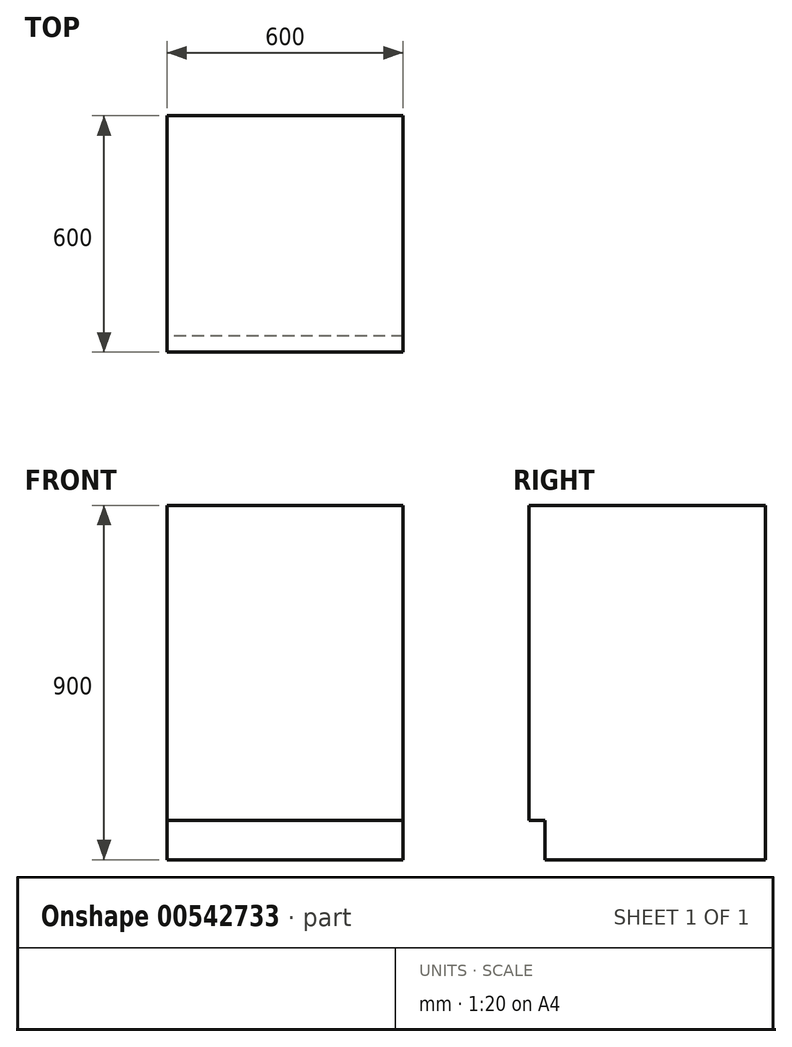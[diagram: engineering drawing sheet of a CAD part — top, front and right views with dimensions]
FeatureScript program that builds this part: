
annotation { "Feature Type Name" : "Feature", "Feature Type Description" : "" }
export const myFeature = defineFeature(function(context is Context, id is Id, definition is map)
    precondition{}
    {
        {
            var Q0;
            Q0=qCreatedBy(makeId("Top.planeOp"),FACE);
            var sketch = newSketch(context, id + "F0", { "sketchPlane" : qUnion([Q0])});
            skLineSegment(sketch, "E0.bottom", {"start": v(300, 300) * mm, "end": v(-300, 300) * mm});
            skLineSegment(sketch, "E0.top", {"start": v(300, -300) * mm, "end": v(-300, -300) * mm});
            skLineSegment(sketch, "E0.left", {"start": v(300, 300) * mm, "end": v(300, -300) * mm});
            skLineSegment(sketch, "E0.right", {"start": v(-300, 300) * mm, "end": v(-300, -300) * mm});
            skPoint(sketch, "E0.middle", {"position": v(0, 0) * mm});
            skSolve(sketch);
        }
        {
            var Q0;
            Q0 = qSketchRegion(id + "F0", true);
            extrude(context, id + "F1", {"entities" : qUnion([Q0]), "depth" : 900 * mm, "offsetDistance" : 25 * mm});
        }
        {
            var Q0;
            Q0=makeQuery(id+"F1.opExtrude","SWEPT_FACE",FACE,{"disambiguationData":[OSD([sQuery(id+"F0.wireOp",EDGE,"E0.top")])]});
            var sketch = newSketch(context, id + "F2", { "sketchPlane" : qUnion([Q0])});
            skLineSegment(sketch, "E1.bottom", {"start": v(-300, 0) * mm, "end": v(300, 0) * mm});
            skLineSegment(sketch, "E1.top", {"start": v(-300, 100) * mm, "end": v(300, 100) * mm});
            skLineSegment(sketch, "E1.left", {"start": v(-300, 0) * mm, "end": v(-300, 100) * mm});
            skLineSegment(sketch, "E1.right", {"start": v(300, 0) * mm, "end": v(300, 100) * mm});
            skSolve(sketch);
        }
        {
            var Q0;
            Q0 = qSketchRegion(id + "F2", true);
            extrude(context, id + "F3", {"entities" : qUnion([Q0]), "operationType" : NewBodyOperationType.REMOVE, "oppositeDirection" : true, "depth" : 40 * mm, "offsetDistance" : 25 * mm});
        }
    });
